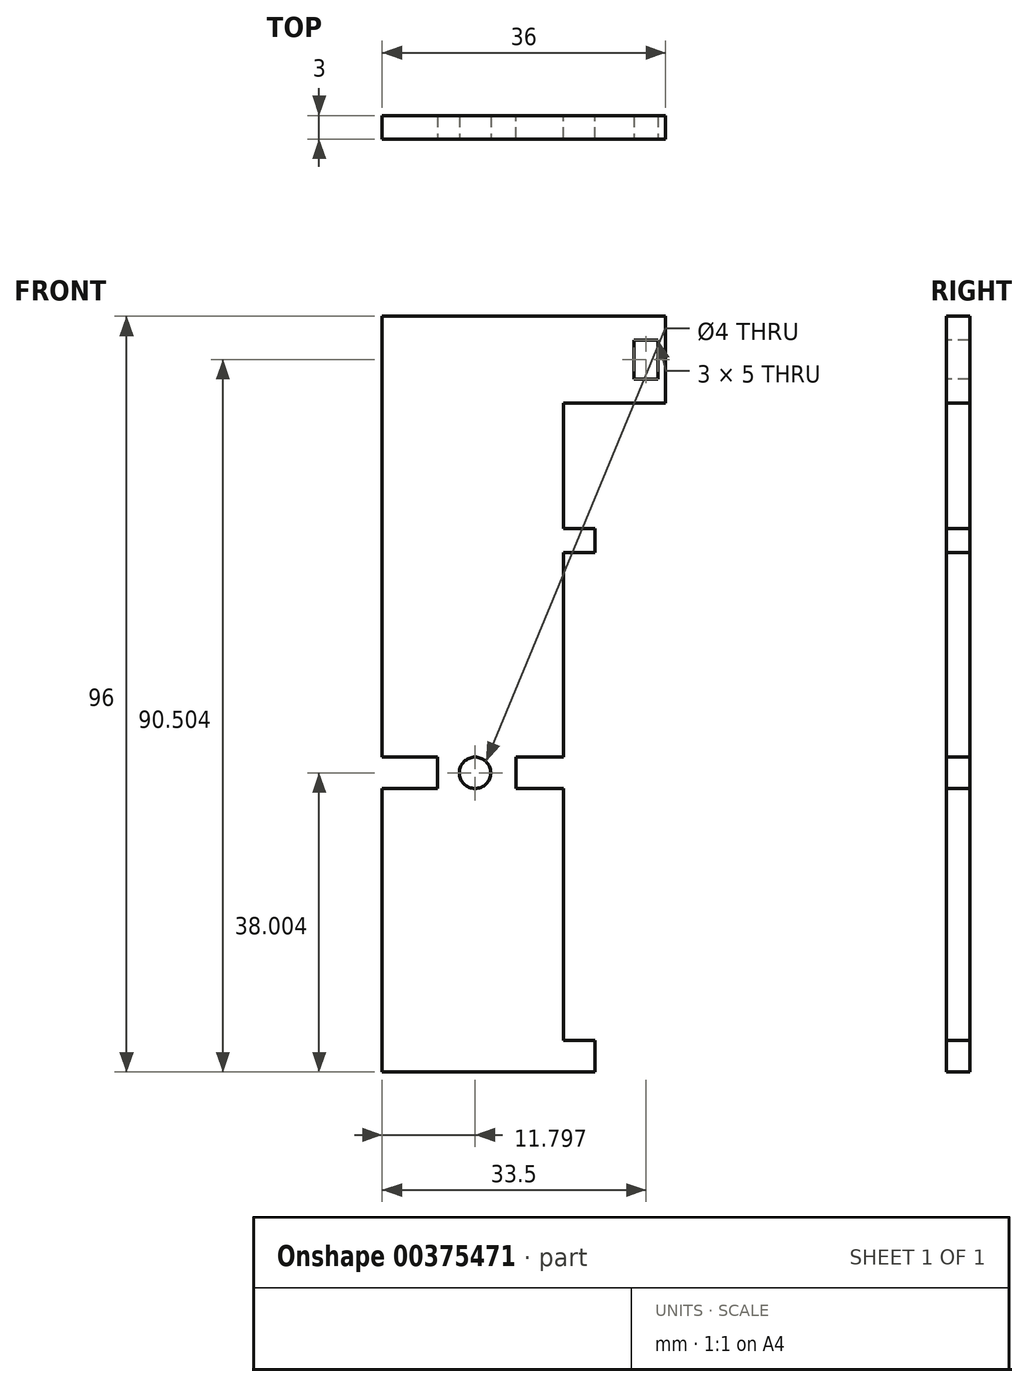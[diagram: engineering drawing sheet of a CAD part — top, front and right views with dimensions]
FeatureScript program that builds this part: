
annotation { "Feature Type Name" : "Feature", "Feature Type Description" : "" }
export const myFeature = defineFeature(function(context is Context, id is Id, definition is map)
    precondition{}
    {
        {
            var Q0;
            Q0=qCreatedBy(makeId("Front.planeOp"),FACE);
            var sketch = newSketch(context, id + "F0", { "sketchPlane" : qUnion([Q0])});
            skLineSegment(sketch, "E0.bottom", {"start": v(-15.03, 38.8) * mm, "end": v(20.97, 38.8) * mm});
            skLineSegment(sketch, "E0.top", {"start": v(-15.03, -57.2) * mm, "end": v(20.97, -57.2) * mm});
            skLineSegment(sketch, "E0.left", {"start": v(-15.03, 38.8) * mm, "end": v(-15.03, -57.2) * mm});
            skLineSegment(sketch, "E0.right", {"start": v(20.97, 38.8) * mm, "end": v(20.97, -57.2) * mm});
            skLineSegment(sketch, "E1", {"start": v(20.97, 38.8) * mm, "end": v(20.97, 27.8) * mm});
            skLineSegment(sketch, "E2", {"start": v(20.97, 27.8) * mm, "end": v(7.97, 27.8) * mm});
            skLineSegment(sketch, "E3", {"start": v(7.97, 27.8) * mm, "end": v(7.97, 11.8) * mm});
            skLineSegment(sketch, "E4", {"start": v(7.97, 11.8) * mm, "end": v(11.97, 11.8) * mm});
            skLineSegment(sketch, "E5", {"start": v(11.97, 11.8) * mm, "end": v(11.97, 8.8) * mm});
            skLineSegment(sketch, "E6", {"start": v(11.97, 8.8) * mm, "end": v(7.97, 8.8) * mm});
            skLineSegment(sketch, "E7", {"start": v(7.97, 8.8) * mm, "end": v(7.97, -17.2) * mm});
            skLineSegment(sketch, "E8", {"start": v(7.97, -17.2) * mm, "end": v(1.97, -17.2) * mm});
            skLineSegment(sketch, "E9", {"start": v(1.97, -17.2) * mm, "end": v(1.97, -21.2) * mm});
            skLineSegment(sketch, "E10", {"start": v(1.97, -21.2) * mm, "end": v(7.97, -21.2) * mm});
            skLineSegment(sketch, "E11", {"start": v(7.97, -53.2) * mm, "end": v(11.97, -53.2) * mm});
            skLineSegment(sketch, "E12", {"start": v(11.97, -53.2) * mm, "end": v(11.97, -57.2) * mm});
            skLineSegment(sketch, "E13", {"start": v(7.97, -53.2) * mm, "end": v(7.97, -21.2) * mm});
            skSolve(sketch);
        }
        {
            var Q0;
            Q0=makeQuery(id+"F0.imprint","IMPRINT",FACE,{"disambiguationData":[TD([[makeQuery(id+"F0.imprint","IMPRINT",EDGE,{"derivedFrom":sQuery(id+"F0.wireOp",EDGE,"E0.bottom")}),-1.0]])]});
            extrude(context, id + "F1", {"entities" : qUnion([Q0]), "depth" : 3 * mm});
        }
        {
            var Q0;
            Q0=makeQuery(id+"F1.opExtrude","CAP_FACE",FACE,{"disambiguationData":[OSD([sQuery(id+"F0.wireOp",EDGE,"E0.bottom"),sQuery(id+"F0.wireOp",EDGE,"E0.top"),sQuery(id+"F0.wireOp",EDGE,"E0.left"),sQuery(id+"F0.wireOp",EDGE,"E1"),sQuery(id+"F0.wireOp",EDGE,"E2"),sQuery(id+"F0.wireOp",EDGE,"E3"),sQuery(id+"F0.wireOp",EDGE,"E4"),sQuery(id+"F0.wireOp",EDGE,"E5"),sQuery(id+"F0.wireOp",EDGE,"E6"),sQuery(id+"F0.wireOp",EDGE,"E7"),sQuery(id+"F0.wireOp",EDGE,"E8"),sQuery(id+"F0.wireOp",EDGE,"E9"),sQuery(id+"F0.wireOp",EDGE,"E10"),sQuery(id+"F0.wireOp",EDGE,"E11"),sQuery(id+"F0.wireOp",EDGE,"E12"),sQuery(id+"F0.wireOp",EDGE,"E13")])],"isStart":false});
            var sketch = newSketch(context, id + "F2", { "sketchPlane" : qUnion([Q0])});
            skLineSegment(sketch, "E14", {"start": v(-15.03, -57.2) * mm, "end": v(-15.03, -21.2) * mm});
            skLineSegment(sketch, "E15", {"start": v(-15.03, -21.2) * mm, "end": v(-8.03, -21.2) * mm});
            skLineSegment(sketch, "E16", {"start": v(-8.03, -21.2) * mm, "end": v(-8.03, -17.2) * mm});
            skLineSegment(sketch, "E17", {"start": v(-8.03, -17.2) * mm, "end": v(-15.03, -17.2) * mm});
            skCircle(sketch, "E18", {"center": v(-3.23, -19.2) * mm, "radius": 2 * mm});
            skPoint(sketch, "E18.centerSnap0", {"position": v(1.97, -19.2) * mm});
            skLineSegment(sketch, "E19", {"start": v(20.97, 38.8) * mm, "end": v(19.97, 38.8) * mm});
            skLineSegment(sketch, "E20", {"start": v(19.97, 38.8) * mm, "end": v(19.97, 35.8) * mm});
            skLineSegment(sketch, "E21", {"start": v(19.97, 35.8) * mm, "end": v(16.97, 35.8) * mm});
            skLineSegment(sketch, "E22", {"start": v(16.97, 35.8) * mm, "end": v(16.97, 30.8) * mm});
            skLineSegment(sketch, "E23", {"start": v(16.97, 30.8) * mm, "end": v(19.97, 30.8) * mm});
            skLineSegment(sketch, "E24", {"start": v(19.97, 30.8) * mm, "end": v(19.97, 35.8) * mm});
            skSolve(sketch);
        }
        {
            var Q0;
            Q0 = qSketchRegion(id + "F2", true);
            var Q1;
            {var subQ0=sQuery(id+"F2.wireOp",EDGE,"E15");Q1=makeQuery(id+"F2.imprint","IMPRINT",FACE,{"disambiguationData":[TD([[makeQuery(id+"F2.imprint","IMPRINT",EDGE,{"derivedFrom":subQ0}),1.0]])]});}
            extrude(context, id + "F3", {"entities" : qUnion([Q0, Q1]), "operationType" : NewBodyOperationType.REMOVE, "oppositeDirection" : true, "depth" : 25 * mm});
        }
    });
